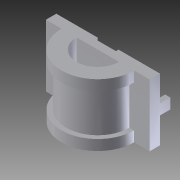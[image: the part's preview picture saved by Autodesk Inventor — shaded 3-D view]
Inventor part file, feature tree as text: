
AUTODESK INVENTOR PART (.ipt)
format: ipt  version: 2015 SP2 (Build 190223200, 223)  size: 150,528 bytes
history: native  units: in
note: dims shown in document units (in); Inventor stores cm internally (conversion verified against a paired STEP export)
features: other x6, extrude x4
ambient origin geometry x8: Origin, YZ Plane, XZ Plane, XY Plane, X Axis, Y Axis, Z Axis, Center Point
bodies: Solid1 (feature_tree)
feature tree (10):
  extrude  "base_extrusion"  Depth=2.0in
  other  "moon_revolution"
  extrude  "cutout_extrusion"  Depth=1.2in
  extrude  "peg_extrusion"  Depth=0.2in TaperAngle=0.0deg
  extrude  "rivet_groove_extrusion"  Depth=0.7in
  other  "base_sketch"
  other  "moon_sketch"
  other  "cutout_sketch"
  other  "peg_sketch"
  other  "rivet_groove_sketch"
